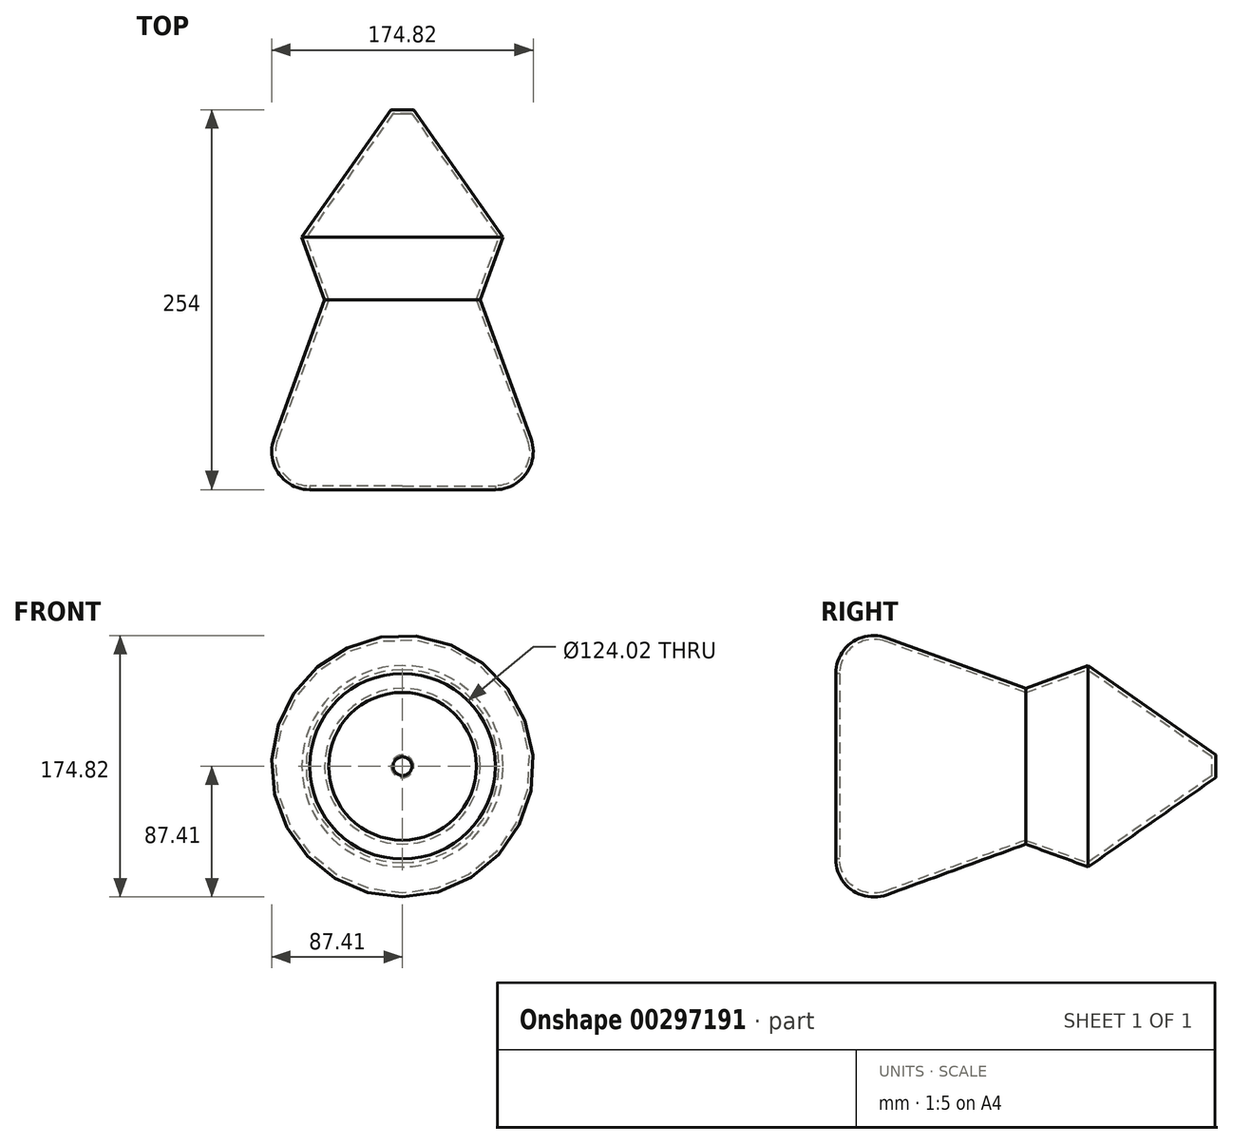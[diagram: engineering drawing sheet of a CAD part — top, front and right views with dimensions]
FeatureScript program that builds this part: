
annotation { "Feature Type Name" : "Feature", "Feature Type Description" : "" }
export const myFeature = defineFeature(function(context is Context, id is Id, definition is map)
    precondition{}
    {
        {
            var Q0;
            Q0=qCreatedBy(makeId("Front.planeOp"),FACE);
            var sketch = newSketch(context, id + "F0", { "sketchPlane" : qUnion([Q0])});
            skCircle(sketch, "E0", {"center": v(0, 0) * mm, "radius": 52.06 * mm});
            skSolve(sketch);
        }
        {
            var Q0;
            Q0=makeQuery(id+"F0.imprint","IMPRINT",FACE,{"disambiguationData":[TD([[makeQuery(id+"F0.imprint","IMPRINT",EDGE,{"derivedFrom":sQuery(id+"F0.wireOp",EDGE,"E0")}),1.0]])]});
            extrude(context, id + "F1", {"entities" : qUnion([Q0]), "endBound" : BoundingType.SYMMETRIC, "depth" : 254 * mm, "hasDraft" : true, "draftAngle" : 20 * degree});
        }
        {
            var Q0;
            Q0=makeQuery(id+"F1.opExtrude","CAP_FACE",FACE,{"disambiguationData":[OSD([sQuery(id+"F0.wireOp",EDGE,"E0")])],"isStart":false});
            fillet(context, id + "F2", {"entities" : qUnion([Q0]), "radius" : 25.4 * mm, "tangentPropagation" : true, "allowEdgeOverflow" : false});
        }
        {
            var Q0;
            Q0=makeQuery(id+"F1.opExtrude","CAP_EDGE",EDGE,{"disambiguationData":[OSD([sQuery(id+"F0.wireOp",EDGE,"E0")])],"isStart":true});
            chamfer(context, id + "F3", {"entities" : qUnion([Q0]), "width" : 63.5 * mm, "tangentPropagation" : true});
        }
        {
            var Q0;
            Q0=makeQuery(id+"F1.opExtrude","CAP_FACE",FACE,{"disambiguationData":[OSD([sQuery(id+"F0.wireOp",EDGE,"E0")])],"isStart":false});
            shell(context, id + "F4", {"entities" : qUnion([Q0]), "thickness" : 2.54 * mm});
        }
    });
